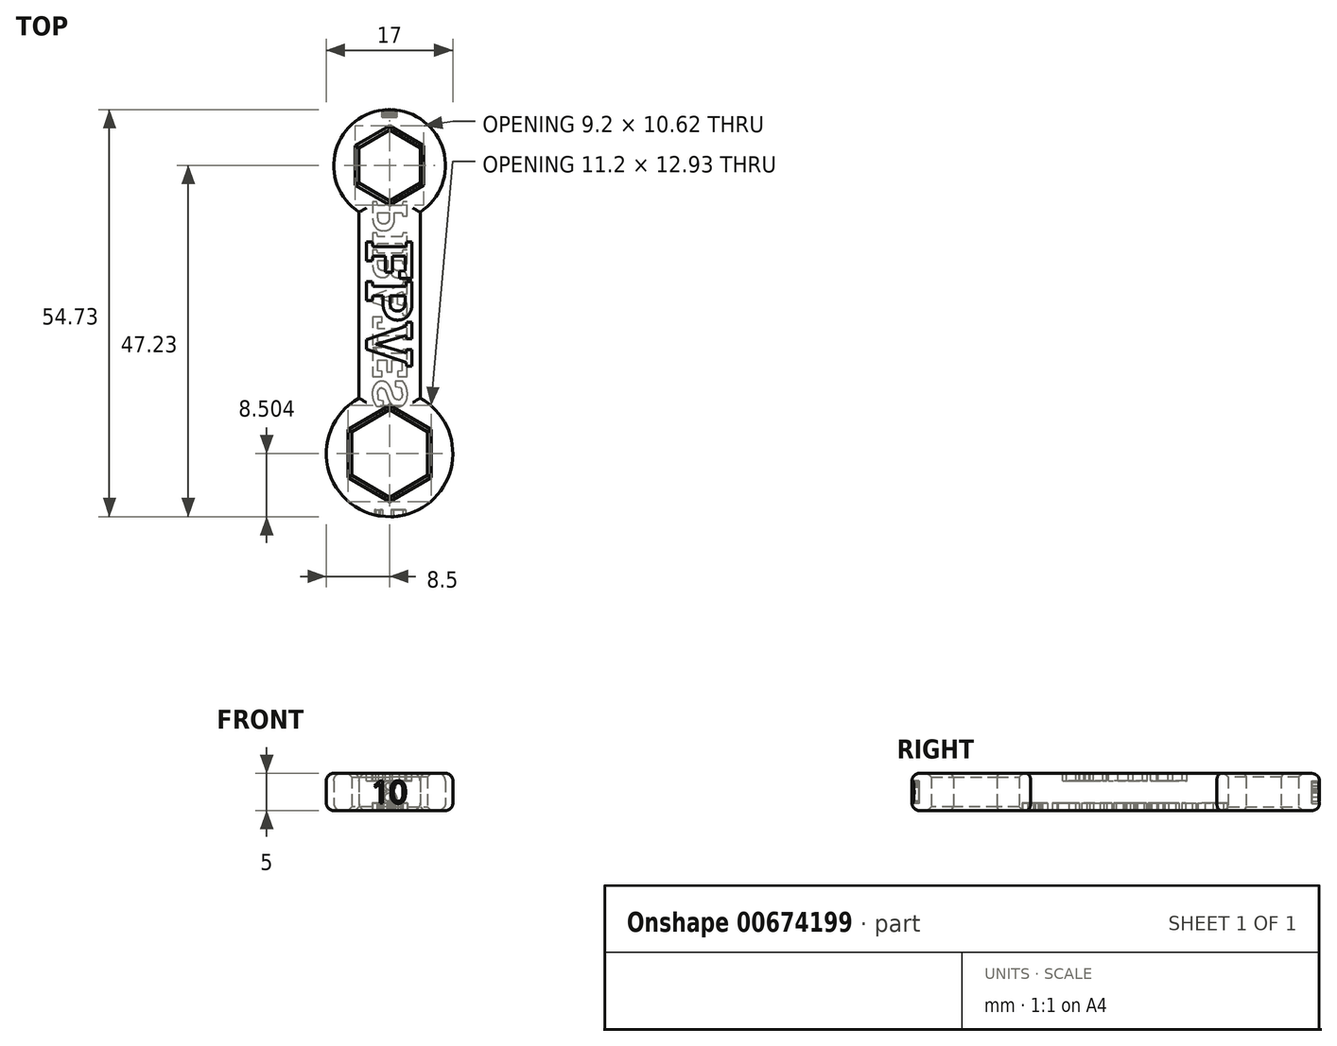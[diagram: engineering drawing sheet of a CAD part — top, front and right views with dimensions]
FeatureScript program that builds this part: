
annotation { "Feature Type Name" : "Feature", "Feature Type Description" : "" }
export const myFeature = defineFeature(function(context is Context, id is Id, definition is map)
    precondition{}
    {
        {
            var Q0;
            Q0=qCreatedBy(makeId("Top.planeOp"),FACE);
            var sketch = newSketch(context, id + "F0", { "sketchPlane" : qUnion([Q0])});
            skCircle(sketch, "E0.cCircle", {"center": v(0, 0) * mm, "radius": 4.1 * mm, "construction": true});
            skLineSegment(sketch, "E0.0", {"start": v(-4.1, -2.37) * mm, "end": v(-4.1, 2.37) * mm});
            skLineSegment(sketch, "E0.1", {"start": v(-4.1, 2.37) * mm, "end": v(0, 4.73) * mm});
            skLineSegment(sketch, "E0.2", {"start": v(0, 4.73) * mm, "end": v(4.1, 2.37) * mm});
            skLineSegment(sketch, "E0.3", {"start": v(4.1, 2.37) * mm, "end": v(4.1, -2.37) * mm});
            skLineSegment(sketch, "E0.4", {"start": v(4.1, -2.37) * mm, "end": v(0, -4.73) * mm});
            skLineSegment(sketch, "E0.5", {"start": v(0, -4.73) * mm, "end": v(-4.1, -2.37) * mm});
            skPoint(sketch, "E0.0.midPoint", {"position": v(-4.1, 0) * mm});
            skCircle(sketch, "E1", {"center": v(0, 0) * mm, "radius": 7.5 * mm});
            skLineSegment(sketch, "E2", {"start": v(-4.1, -6.28) * mm, "end": v(-4.1, -31.28) * mm});
            skLineSegment(sketch, "E3", {"start": v(4.1, -6.28) * mm, "end": v(4.1, -31.28) * mm});
            skLineSegment(sketch, "E4", {"start": v(-4.1, -31.28) * mm, "end": v(4.1, -31.28) * mm});
            skLineSegment(sketch, "E5", {"start": v(0, -31.28) * mm, "end": v(0, -38.73) * mm, "construction": true});
            skCircle(sketch, "E6", {"center": v(0, -38.73) * mm, "radius": 8.5 * mm});
            skCircle(sketch, "E7.cCircle", {"center": v(0, -38.73) * mm, "radius": 5.1 * mm, "construction": true});
            skLineSegment(sketch, "E7.0", {"start": v(5.1, -35.78) * mm, "end": v(5.1, -41.67) * mm});
            skLineSegment(sketch, "E7.1", {"start": v(5.1, -41.67) * mm, "end": v(0, -44.61) * mm});
            skLineSegment(sketch, "E7.2", {"start": v(0, -44.61) * mm, "end": v(-5.1, -41.67) * mm});
            skLineSegment(sketch, "E7.3", {"start": v(-5.1, -41.67) * mm, "end": v(-5.1, -35.78) * mm});
            skLineSegment(sketch, "E7.4", {"start": v(-5.1, -35.78) * mm, "end": v(0, -32.84) * mm});
            skLineSegment(sketch, "E7.5", {"start": v(0, -32.84) * mm, "end": v(5.1, -35.78) * mm});
            skPoint(sketch, "E7.0.midPoint", {"position": v(5.1, -38.73) * mm});
            skSolve(sketch);
        }
        {
            var Q0;
            Q0=makeQuery(id+"F0.imprint","IMPRINT",FACE,{"disambiguationData":[TD([[makeQuery(id+"F0.imprint","IMPRINT",EDGE,{"derivedFrom":sQuery(id+"F0.wireOp",EDGE,"E0.0")}),1.0]])]});
            var Q1;
            {var subQ0=sQuery(id+"F0.wireOp",EDGE,"E2");Q1=makeQuery(id+"F0.imprint","IMPRINT",FACE,{"disambiguationData":[TD([[makeQuery(id+"F0.imprint","IMPRINT",EDGE,{"derivedFrom":subQ0}),1.0]])]});}
            var Q2;
            {var subQ1=sQuery(id+"F0.wireOp",EDGE,"E4");Q2=makeQuery(id+"F0.imprint","IMPRINT",FACE,{"disambiguationData":[TD([[makeQuery(id+"F0.imprint","IMPRINT",EDGE,{"derivedFrom":subQ1}),-1.0]])]});}
            var Q3;
            {var subQ0=sQuery(id+"F0.wireOp",EDGE,"E4");Q3=makeQuery(id+"F0.imprint","IMPRINT",FACE,{"disambiguationData":[TD([[makeQuery(id+"F0.imprint","IMPRINT",EDGE,{"derivedFrom":subQ0}),1.0]])]});}
            extrude(context, id + "F1", {"entities" : qUnion([Q0, Q1, Q2, Q3]), "depth" : 5 * mm, "offsetDistance" : 25 * mm});
        }
        {
            var Q0;
            Q0=makeQuery(id+"F1.opExtrude","CAP_FACE",FACE,{"disambiguationData":[OSD([sQuery(id+"F0.wireOp",EDGE,"E0.0"),sQuery(id+"F0.wireOp",EDGE,"E0.1"),sQuery(id+"F0.wireOp",EDGE,"E0.2"),sQuery(id+"F0.wireOp",EDGE,"E0.3"),sQuery(id+"F0.wireOp",EDGE,"E0.4"),sQuery(id+"F0.wireOp",EDGE,"E0.5"),sQuery(id+"F0.wireOp",EDGE,"E1"),sQuery(id+"F0.wireOp",EDGE,"E2"),sQuery(id+"F0.wireOp",EDGE,"E3"),sQuery(id+"F0.wireOp",EDGE,"E6"),sQuery(id+"F0.wireOp",EDGE,"E7.0"),sQuery(id+"F0.wireOp",EDGE,"E7.1"),sQuery(id+"F0.wireOp",EDGE,"E7.2"),sQuery(id+"F0.wireOp",EDGE,"E7.3"),sQuery(id+"F0.wireOp",EDGE,"E7.4"),sQuery(id+"F0.wireOp",EDGE,"E7.5")])],"isStart":false});
            var sketch = newSketch(context, id + "F2", { "sketchPlane" : qUnion([Q0])});
            skText(sketch, "E8", { "text": "FPV", "fontName": "RobotoSlab-Bold.ttf"});
            skLineSegment(sketch, "E9", {"start": v(0, -4.73) * mm, "end": v(0, -10.06) * mm, "construction": true});
            skLineSegment(sketch, "E10", {"start": v(0, -32.84) * mm, "end": v(0, -27.51) * mm, "construction": true});
            const initialGuessF2  = {"E8": [-0.0031, -0.01006, 0, -1, 0.0062]};
            skSetInitialGuess(sketch, initialGuessF2);
            skSolve(sketch);
        }
        {
            var Q0;
            Q0 = qSketchRegion(id + "F2", true);
            extrude(context, id + "F3", {"entities" : qUnion([Q0]), "operationType" : NewBodyOperationType.REMOVE, "oppositeDirection" : true, "depth" : 1 * mm, "offsetDistance" : 25 * mm});
        }
        {
            var Q0;
            Q0=makeQuery(id+"F1.opExtrude","CAP_FACE",FACE,{"disambiguationData":[OSD([sQuery(id+"F0.wireOp",EDGE,"E0.0"),sQuery(id+"F0.wireOp",EDGE,"E0.1"),sQuery(id+"F0.wireOp",EDGE,"E0.2"),sQuery(id+"F0.wireOp",EDGE,"E0.3"),sQuery(id+"F0.wireOp",EDGE,"E0.4"),sQuery(id+"F0.wireOp",EDGE,"E0.5"),sQuery(id+"F0.wireOp",EDGE,"E1"),sQuery(id+"F0.wireOp",EDGE,"E2"),sQuery(id+"F0.wireOp",EDGE,"E3"),sQuery(id+"F0.wireOp",EDGE,"E6"),sQuery(id+"F0.wireOp",EDGE,"E7.0"),sQuery(id+"F0.wireOp",EDGE,"E7.1"),sQuery(id+"F0.wireOp",EDGE,"E7.2"),sQuery(id+"F0.wireOp",EDGE,"E7.3"),sQuery(id+"F0.wireOp",EDGE,"E7.4"),sQuery(id+"F0.wireOp",EDGE,"E7.5")])],"isStart":true});
            var sketch = newSketch(context, id + "F4", { "sketchPlane" : qUnion([Q0])});
            skText(sketch, "E11", { "text": "PIRATES", "fontName": "RobotoSlab-Bold.ttf"});
            skLineSegment(sketch, "E12", {"start": v(-2.33, 18.79) * mm, "end": v(-4.1, 18.79) * mm, "construction": true});
            skPoint(sketch, "E12.endSnap0", {"position": v(-4.1, 18.78) * mm});
            skLineSegment(sketch, "E13", {"start": v(2.33, 18.79) * mm, "end": v(4.1, 18.79) * mm, "construction": true});
            const initialGuessF4  = {"E11": [0.00233, 0.00473, 0, 1, 0.00465]};
            skSetInitialGuess(sketch, initialGuessF4);
            skSolve(sketch);
        }
        {
            var Q0;
            Q0 = qSketchRegion(id + "F4", true);
            extrude(context, id + "F5", {"entities" : qUnion([Q0]), "operationType" : NewBodyOperationType.REMOVE, "oppositeDirection" : true, "depth" : 1 * mm, "offsetDistance" : 25 * mm});
        }
        {
            var Q0;
            Q0=qCreatedBy(makeId("Front.planeOp"),FACE);
            cPlane(context, id + "F6", {"entities" : qUnion([Q0]), "cplaneType" : CPlaneType.OFFSET, "offset" : 7.5 * mm, "oppositeDirection" : true, "width" : 150 * mm, "height" : 150 * mm});
        }
        {
            var Q0;
            Q0=qCreatedBy(id+"F6.planeOp",FACE);
            var sketch = newSketch(context, id + "F7", { "sketchPlane" : qUnion([Q0])});
            skText(sketch, "E14", { "text": "8", "fontName": "OpenSans-Regular.ttf"});
            const initialGuessF7  = {"E14": [-0.00122, 0.001, 1, 0, 0.003]};
            skSetInitialGuess(sketch, initialGuessF7);
            skSolve(sketch);
        }
        {
            var Q0;
            Q0 = qSketchRegion(id + "F7", true);
            extrude(context, id + "F8", {"entities" : qUnion([Q0]), "operationType" : NewBodyOperationType.REMOVE, "depth" : 1 * mm, "offsetDistance" : 25 * mm});
        }
        {
            var Q0;
            Q0=qCreatedBy(makeId("Front.planeOp"),FACE);
            cPlane(context, id + "F9", {"entities" : qUnion([Q0]), "cplaneType" : CPlaneType.OFFSET, "offset" : 47.3 * mm, "width" : 150 * mm, "height" : 150 * mm});
        }
        {
            var Q0;
            Q0=qCreatedBy(id+"F9.planeOp",FACE);
            var sketch = newSketch(context, id + "F10", { "sketchPlane" : qUnion([Q0])});
            skText(sketch, "E15", { "text": "10", "fontName": "OpenSans-Regular.ttf"});
            const initialGuessF10  = {"E15": [-0.00241, 0.001, 1, 0, 0.003]};
            skSetInitialGuess(sketch, initialGuessF10);
            skSolve(sketch);
        }
        {
            var Q0;
            Q0 = qSketchRegion(id + "F10", true);
            extrude(context, id + "F11", {"entities" : qUnion([Q0]), "operationType" : NewBodyOperationType.REMOVE, "oppositeDirection" : true, "depth" : 1 * mm, "offsetDistance" : 25 * mm});
        }
        {
            var Q0;
            Q0=makeQuery(id+"F1.opExtrude","CAP_EDGE",EDGE,{"disambiguationData":[OSD([sQuery(id+"F0.wireOp",EDGE,"E2")])],"isStart":false});
            var Q1;
            Q1=makeQuery(id+"F1.opExtrude","CAP_EDGE",EDGE,{"disambiguationData":[OSD([sQuery(id+"F0.wireOp",EDGE,"E3")])],"isStart":false});
            var Q2;
            Q2=makeQuery(id+"F1.opExtrude","CAP_EDGE",EDGE,{"disambiguationData":[OSD([sQuery(id+"F0.wireOp",EDGE,"E1")])],"isStart":false});
            var Q3;
            Q3=makeQuery(id+"F1.opExtrude","CAP_EDGE",EDGE,{"disambiguationData":[OSD([sQuery(id+"F0.wireOp",EDGE,"E6")])],"isStart":false});
            var Q4;
            Q4=makeQuery(id+"F1.opExtrude","CAP_EDGE",EDGE,{"disambiguationData":[OSD([sQuery(id+"F0.wireOp",EDGE,"E2")])],"isStart":true});
            var Q5;
            Q5=makeQuery(id+"F1.opExtrude","CAP_EDGE",EDGE,{"disambiguationData":[OSD([sQuery(id+"F0.wireOp",EDGE,"E1")])],"isStart":true});
            var Q6;
            Q6=makeQuery(id+"F1.opExtrude","CAP_EDGE",EDGE,{"disambiguationData":[OSD([sQuery(id+"F0.wireOp",EDGE,"E6")])],"isStart":true});
            var Q7;
            Q7=makeQuery(id+"F1.opExtrude","CAP_EDGE",EDGE,{"disambiguationData":[OSD([sQuery(id+"F0.wireOp",EDGE,"E3")])],"isStart":true});
            fillet(context, id + "F12", {"entities" : qUnion([Q0, Q1, Q2, Q3, Q4, Q5, Q6, Q7]), "radius" : 1 * mm, "tangentPropagation" : true, "allowEdgeOverflow" : false});
        }
        {
            var Q0;
            Q0=makeQuery(id+"F1.opExtrude","CAP_EDGE",EDGE,{"disambiguationData":[OSD([sQuery(id+"F0.wireOp",EDGE,"E7.3")])],"isStart":false});
            var Q1;
            Q1=makeQuery(id+"F1.opExtrude","CAP_EDGE",EDGE,{"disambiguationData":[OSD([sQuery(id+"F0.wireOp",EDGE,"E7.4")])],"isStart":false});
            var Q2;
            Q2=makeQuery(id+"F1.opExtrude","CAP_EDGE",EDGE,{"disambiguationData":[OSD([sQuery(id+"F0.wireOp",EDGE,"E7.5")])],"isStart":false});
            var Q3;
            Q3=makeQuery(id+"F1.opExtrude","CAP_EDGE",EDGE,{"disambiguationData":[OSD([sQuery(id+"F0.wireOp",EDGE,"E7.0")])],"isStart":false});
            var Q4;
            Q4=makeQuery(id+"F1.opExtrude","CAP_EDGE",EDGE,{"disambiguationData":[OSD([sQuery(id+"F0.wireOp",EDGE,"E7.1")])],"isStart":false});
            var Q5;
            Q5=makeQuery(id+"F1.opExtrude","CAP_EDGE",EDGE,{"disambiguationData":[OSD([sQuery(id+"F0.wireOp",EDGE,"E7.2")])],"isStart":false});
            var Q6;
            Q6=makeQuery(id+"F1.opExtrude","CAP_EDGE",EDGE,{"disambiguationData":[OSD([sQuery(id+"F0.wireOp",EDGE,"E7.0")])],"isStart":true});
            var Q7;
            Q7=makeQuery(id+"F1.opExtrude","CAP_EDGE",EDGE,{"disambiguationData":[OSD([sQuery(id+"F0.wireOp",EDGE,"E7.1")])],"isStart":true});
            var Q8;
            Q8=makeQuery(id+"F1.opExtrude","CAP_EDGE",EDGE,{"disambiguationData":[OSD([sQuery(id+"F0.wireOp",EDGE,"E7.2")])],"isStart":true});
            var Q9;
            Q9=makeQuery(id+"F1.opExtrude","CAP_EDGE",EDGE,{"disambiguationData":[OSD([sQuery(id+"F0.wireOp",EDGE,"E7.3")])],"isStart":true});
            var Q10;
            Q10=makeQuery(id+"F1.opExtrude","CAP_EDGE",EDGE,{"disambiguationData":[OSD([sQuery(id+"F0.wireOp",EDGE,"E7.4")])],"isStart":true});
            var Q11;
            Q11=makeQuery(id+"F1.opExtrude","CAP_EDGE",EDGE,{"disambiguationData":[OSD([sQuery(id+"F0.wireOp",EDGE,"E7.5")])],"isStart":true});
            var Q12;
            Q12=makeQuery(id+"F1.opExtrude","CAP_EDGE",EDGE,{"disambiguationData":[OSD([sQuery(id+"F0.wireOp",EDGE,"E0.5")])],"isStart":true});
            var Q13;
            Q13=makeQuery(id+"F1.opExtrude","CAP_EDGE",EDGE,{"disambiguationData":[OSD([sQuery(id+"F0.wireOp",EDGE,"E0.0")])],"isStart":true});
            var Q14;
            Q14=makeQuery(id+"F1.opExtrude","CAP_EDGE",EDGE,{"disambiguationData":[OSD([sQuery(id+"F0.wireOp",EDGE,"E0.1")])],"isStart":true});
            var Q15;
            Q15=makeQuery(id+"F1.opExtrude","CAP_EDGE",EDGE,{"disambiguationData":[OSD([sQuery(id+"F0.wireOp",EDGE,"E0.2")])],"isStart":true});
            var Q16;
            Q16=makeQuery(id+"F1.opExtrude","CAP_EDGE",EDGE,{"disambiguationData":[OSD([sQuery(id+"F0.wireOp",EDGE,"E0.3")])],"isStart":true});
            var Q17;
            Q17=makeQuery(id+"F1.opExtrude","CAP_EDGE",EDGE,{"disambiguationData":[OSD([sQuery(id+"F0.wireOp",EDGE,"E0.4")])],"isStart":true});
            var Q18;
            Q18=makeQuery(id+"F1.opExtrude","CAP_EDGE",EDGE,{"disambiguationData":[OSD([sQuery(id+"F0.wireOp",EDGE,"E0.0")])],"isStart":false});
            var Q19;
            Q19=makeQuery(id+"F1.opExtrude","CAP_EDGE",EDGE,{"disambiguationData":[OSD([sQuery(id+"F0.wireOp",EDGE,"E0.1")])],"isStart":false});
            var Q20;
            Q20=makeQuery(id+"F1.opExtrude","CAP_EDGE",EDGE,{"disambiguationData":[OSD([sQuery(id+"F0.wireOp",EDGE,"E0.2")])],"isStart":false});
            var Q21;
            Q21=makeQuery(id+"F1.opExtrude","CAP_EDGE",EDGE,{"disambiguationData":[OSD([sQuery(id+"F0.wireOp",EDGE,"E0.3")])],"isStart":false});
            var Q22;
            Q22=makeQuery(id+"F1.opExtrude","CAP_EDGE",EDGE,{"disambiguationData":[OSD([sQuery(id+"F0.wireOp",EDGE,"E0.4")])],"isStart":false});
            var Q23;
            Q23=makeQuery(id+"F1.opExtrude","CAP_EDGE",EDGE,{"disambiguationData":[OSD([sQuery(id+"F0.wireOp",EDGE,"E0.5")])],"isStart":false});
            chamfer(context, id + "F13", {"entities" : qUnion([Q0, Q1, Q2, Q3, Q4, Q5, Q6, Q7, Q8, Q9, Q10, Q11, Q12, Q13, Q14, Q15, Q16, Q17, Q18, Q19, Q20, Q21, Q22, Q23]), "width" : .5 * mm, "tangentPropagation" : true});
        }
    });
